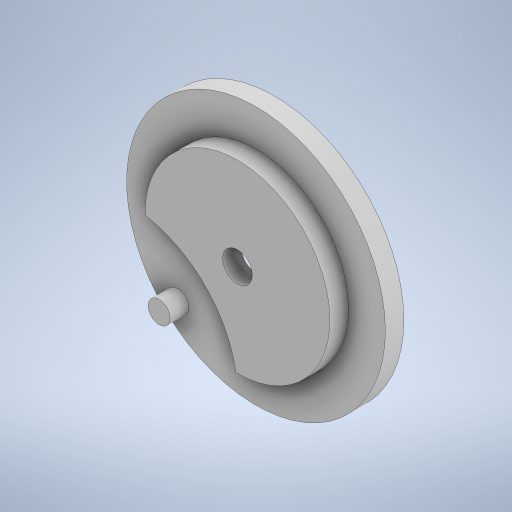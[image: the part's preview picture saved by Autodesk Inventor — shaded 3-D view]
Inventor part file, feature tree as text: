
AUTODESK INVENTOR PART (.ipt)
format: ipt  version: 2024 (Build 280153000, 153)  size: 265,216 bytes
history: native  units: mm
features: extrude x2, sketch x1
ambient origin geometry x8: Origin, YZ Plane, XZ Plane, XY Plane, X Axis, Y Axis, Z Axis, Center Point
bodies: Solid1 (feature_tree)
feature tree (3):
  sketch  "Sketch1"  dims[d0=30.0mm d1=30.0mm d2=60.0mm d3=60.0mm d4=50.0mm d5=70.0mm d6=8.0mm d7=6.0mm d8=5.0mm d9=0.0mm d10=5.0mm d11=0.0mm]
  extrude  "Extrusion1"  Depth=30.0mm
  extrude  "Extrusion2"  Depth=5.0mm
